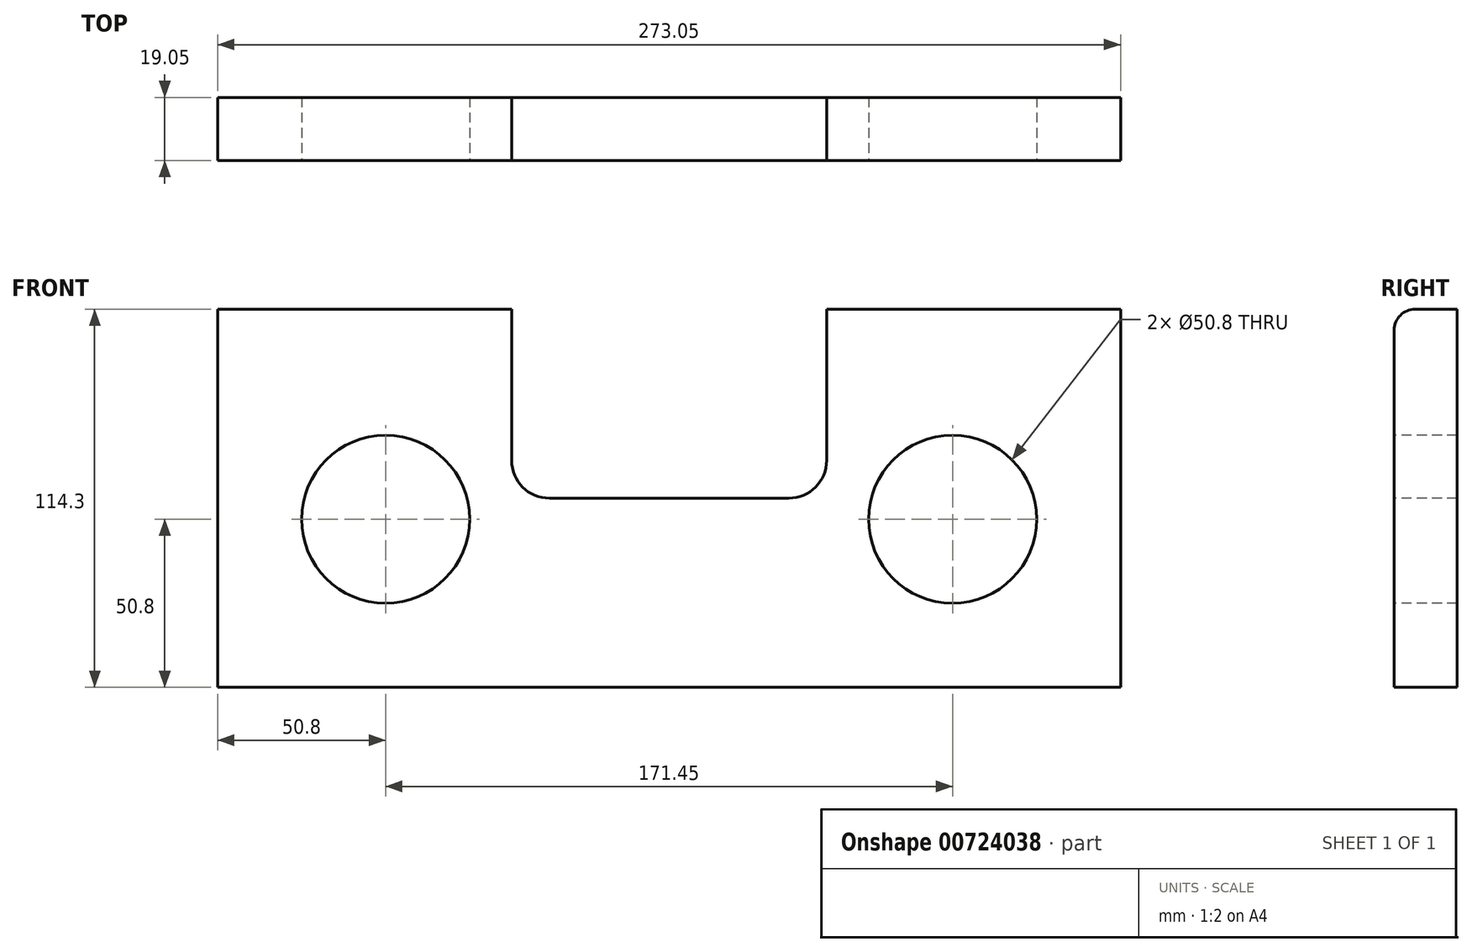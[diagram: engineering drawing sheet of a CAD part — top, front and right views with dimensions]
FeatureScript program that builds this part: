
annotation { "Feature Type Name" : "Feature", "Feature Type Description" : "" }
export const myFeature = defineFeature(function(context is Context, id is Id, definition is map)
    precondition{}
    {
        {
            var Q0;
            Q0=qCreatedBy(makeId("Front.planeOp"),FACE);
            var sketch = newSketch(context, id + "F0", { "sketchPlane" : qUnion([Q0])});
            skLineSegment(sketch, "E0.bottom", {"start": v(0, 0) * mm, "end": v(273.05, 0) * mm});
            skLineSegment(sketch, "E0.top", {"start": v(0, 114.3) * mm, "end": v(273.05, 114.3) * mm});
            skLineSegment(sketch, "E0.left", {"start": v(0, 0) * mm, "end": v(0, 114.3) * mm});
            skLineSegment(sketch, "E0.right", {"start": v(273.05, 0) * mm, "end": v(273.05, 114.3) * mm});
            skSolve(sketch);
        }
        {
            var Q0;
            Q0=qSketchRegion(id+"F0",true);
            extrude(context, id + "F1", {"entities" : qUnion([Q0]), "depth" : 19.05 * mm, "offsetDistance" : 25.4 * mm});
        }
        {
            var Q0;
            Q0=makeQuery(id+"F1.opExtrude","CAP_FACE",FACE,{"disambiguationData":[OSD([sQuery(id+"F0.wireOp",EDGE,"E0.bottom"),sQuery(id+"F0.wireOp",EDGE,"E0.top"),sQuery(id+"F0.wireOp",EDGE,"E0.left"),sQuery(id+"F0.wireOp",EDGE,"E0.right")])],"isStart":false});
            var sketch = newSketch(context, id + "F2", { "sketchPlane" : qUnion([Q0])});
            skCircle(sketch, "E1", {"center": v(50.8, 50.8) * mm, "radius": 25.4 * mm});
            skCircle(sketch, "E2", {"center": v(222.25, 50.8) * mm, "radius": 25.4 * mm});
            skLineSegment(sketch, "E3", {"start": v(88.9, 114.3) * mm, "end": v(88.9, 68.58) * mm});
            skLineSegment(sketch, "E4", {"start": v(100.33, 57.15) * mm, "end": v(172.72, 57.15) * mm});
            skLineSegment(sketch, "E5", {"start": v(184.15, 68.58) * mm, "end": v(184.15, 114.3) * mm});
            skPoint(sketch, "E6.visualSharp", {"position": v(88.9, 57.15) * mm});
            skArc(sketch, "E6.filletArc", {"start": v(88.9, 68.58) * mm, "mid": v(92.25, 60.5) * mm, "end": v(100.33, 57.15) * mm});
            skPoint(sketch, "E7.visualSharp", {"position": v(184.15, 57.15) * mm});
            skArc(sketch, "E7.filletArc", {"start": v(172.72, 57.15) * mm, "mid": v(180.8, 60.5) * mm, "end": v(184.15, 68.58) * mm});
            skLineSegment(sketch, "E8", {"start": v(151.05, 57.15) * mm, "end": v(151.05, 38.12) * mm});
            skLineSegment(sketch, "E9", {"start": v(151.05, 38.12) * mm, "end": v(64.33, 38.12) * mm});
            skLineSegment(sketch, "E10", {"start": v(64.33, 38.12) * mm, "end": v(51.78, 25.42) * mm});
            skLineSegment(sketch, "E11", {"start": v(51.78, 25.42) * mm, "end": v(223.23, 25.42) * mm});
            skLineSegment(sketch, "E12", {"start": v(223.23, 25.42) * mm, "end": v(207.7, 38.12) * mm});
            skLineSegment(sketch, "E13", {"start": v(207.7, 38.12) * mm, "end": v(176.45, 38.12) * mm});
            skLineSegment(sketch, "E14", {"start": v(176.45, 38.12) * mm, "end": v(176.45, 57.15) * mm});
            skSolve(sketch);
        }
        {
            var Q0;
            Q0=qSketchRegion(id+"F2",true);
            var Q1;
            {var subQ5=sQuery(id+"F2.wireOp",EDGE,"E3");Q1=makeQuery(id+"F2.imprint","IMPRINT",FACE,{"disambiguationData":[TD([[makeQuery(id+"F2.imprint","IMPRINT",EDGE,{"derivedFrom":subQ5}),1.0]])]});}
            extrude(context, id + "F3", {"entities" : qUnion([Q0, Q1]), "operationType" : NewBodyOperationType.REMOVE, "oppositeDirection" : true, "depth" : 25.4 * mm, "offsetDistance" : 25.4 * mm});
        }
        {
            var Q0;
            Q0 = qSketchRegion(id + "F2", true);
            extrude(context, id + "F4", {"entities" : qUnion([Q0]), "operationType" : NewBodyOperationType.REMOVE, "oppositeDirection" : true, "depth" : 25.4 * mm, "offsetDistance" : 25.4 * mm});
        }
        {
            var Q0;
            {var subQ0=sQuery(id+"F0.wireOp",EDGE,"E0.left");var subQ1=sQuery(id+"F0.wireOp",EDGE,"E0.top");Q0=makeQuery(id+"F3.boolean.opBoolean","SPLIT",EDGE,{"disambiguationData":[TD([makeQuery(id+"F1.opExtrude","SWEPT_FACE",FACE,{"disambiguationData":[OSD([subQ0])]})])],"derivedFrom":makeQuery(id+"F1.opExtrude","CAP_EDGE",EDGE,{"disambiguationData":[OSD([subQ1])],"isStart":false})});}
            fillet(context, id + "F5", {"entities" : qUnion([Q0]), "radius" : 6.35 * mm, "tangentPropagation" : true, "allowEdgeOverflow" : false});
        }
        {
            var Q0;
            {var subQ0=sQuery(id+"F0.wireOp",EDGE,"E0.right");var subQ1=sQuery(id+"F0.wireOp",EDGE,"E0.top");Q0=makeQuery(id+"F3.boolean.opBoolean","SPLIT",EDGE,{"disambiguationData":[TD([makeQuery(id+"F1.opExtrude","SWEPT_FACE",FACE,{"disambiguationData":[OSD([subQ0])]})])],"derivedFrom":makeQuery(id+"F1.opExtrude","CAP_EDGE",EDGE,{"disambiguationData":[OSD([subQ1])],"isStart":false})});}
            fillet(context, id + "F6", {"entities" : qUnion([Q0]), "radius" : 6.35 * mm, "tangentPropagation" : true, "allowEdgeOverflow" : false});
        }
    });
